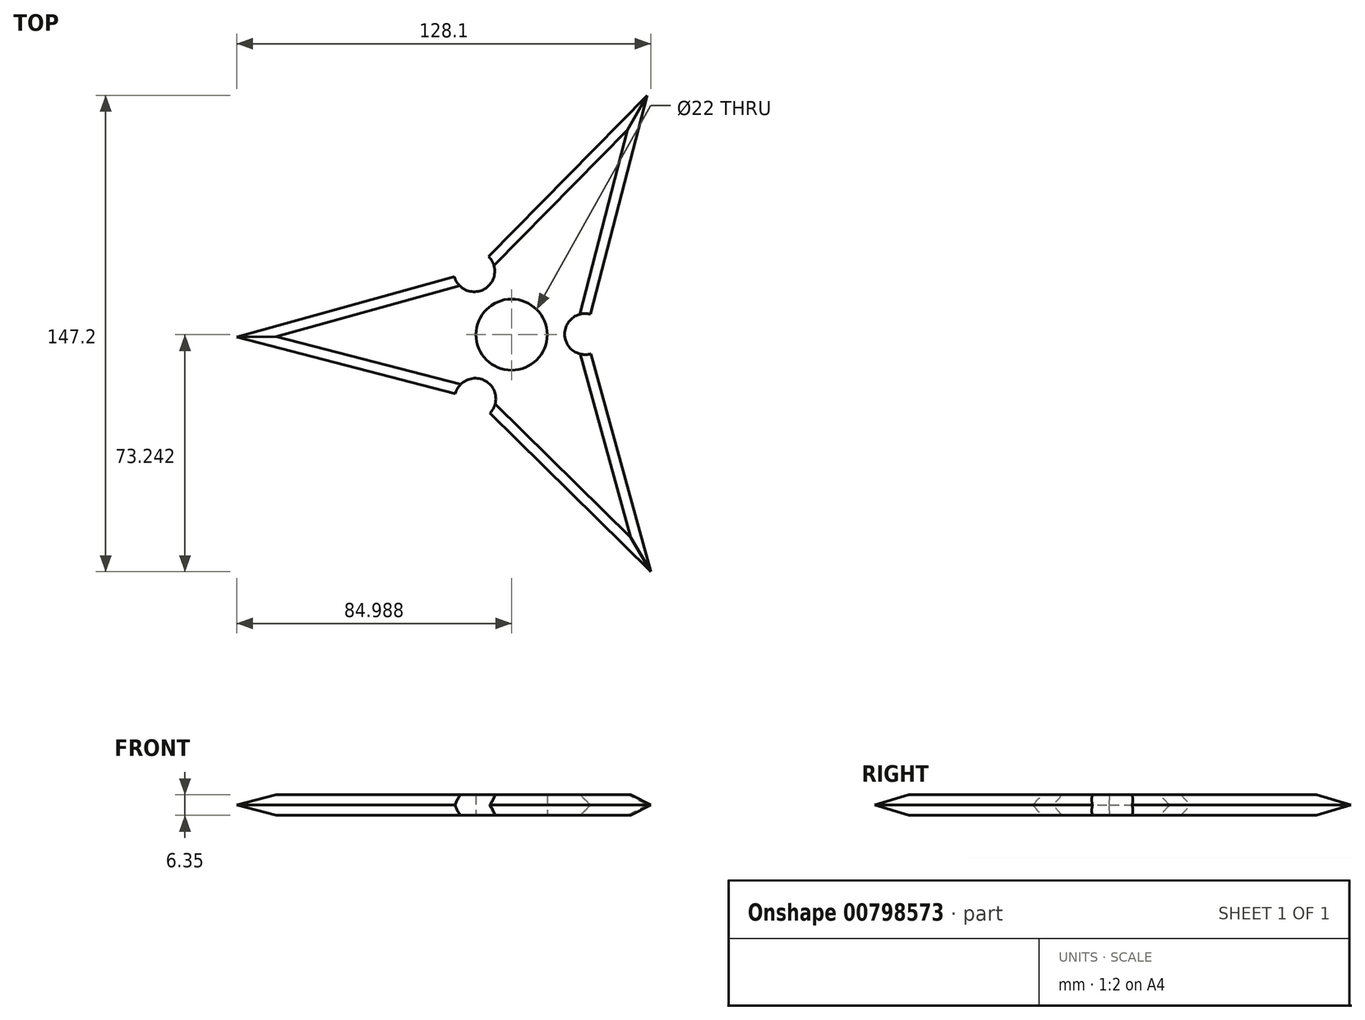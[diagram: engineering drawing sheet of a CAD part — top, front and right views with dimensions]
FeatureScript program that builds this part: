
annotation { "Feature Type Name" : "Feature", "Feature Type Description" : "" }
export const myFeature = defineFeature(function(context is Context, id is Id, definition is map)
    precondition{}
    {
        {
            var Q0;
            Q0=qCreatedBy(makeId("Top.planeOp"),FACE);
            var sketch = newSketch(context, id + "F0", { "sketchPlane" : qUnion([Q0])});
            skLineSegment(sketch, "E0", {"start": v(19.1, 47.74) * mm, "end": v(-34.32, -6.6) * mm});
            skLineSegment(sketch, "E1", {"start": v(-34.32, -6.6) * mm, "end": v(-107.76, -26.93) * mm});
            skLineSegment(sketch, "E2", {"start": v(-107.76, -26.93) * mm, "end": v(-34, -46.04) * mm});
            skLineSegment(sketch, "E3", {"start": v(-34, -46.04) * mm, "end": v(20.34, -99.46) * mm});
            skLineSegment(sketch, "E4", {"start": v(20.34, -99.46) * mm, "end": v(0, -26.03) * mm});
            skLineSegment(sketch, "E5", {"start": v(0, -26.03) * mm, "end": v(19.1, 47.74) * mm});
            skLineSegment(sketch, "E6", {"start": v(-34.32, -6.6) * mm, "end": v(20.34, -99.46) * mm});
            skLineSegment(sketch, "E7", {"start": v(-34, -46.04) * mm, "end": v(19.1, 47.74) * mm});
            skLineSegment(sketch, "E8", {"start": v(0, -26.03) * mm, "end": v(-107.76, -26.93) * mm});
            skCircle(sketch, "E9", {"center": v(-34.32, -6.6) * mm, "radius": 6.35 * mm});
            skCircle(sketch, "E10", {"center": v(-22.77, -26.22) * mm, "radius": 11 * mm});
            skCircle(sketch, "E11", {"center": v(0, -26.03) * mm, "radius": 6.35 * mm});
            skCircle(sketch, "E12", {"center": v(-34, -46.04) * mm, "radius": 6.35 * mm});
            skSolve(sketch);
        }
        {
            var Q0;
            {var subQ0=sQuery(id+"F0.wireOp",EDGE,"E9");var subQ3=sQuery(id+"F0.wireOp",EDGE,"E6");var subQ4=makeQuery(id+"F0.imprint","INTERSECT",VERTEX,{"derivedFrom":[subQ3,subQ0]});Q0=makeQuery(id+"F0.imprint","IMPRINT",FACE,{"disambiguationData":[TD([[makeQuery(id+"F0.imprint","IMPRINT",EDGE,{"disambiguationData":[TD([[subQ4,-1.0]])],"derivedFrom":subQ3}),1.0]])]});}
            var Q1;
            {var subQ5=sQuery(id+"F0.wireOp",EDGE,"E9");var subQ7=sQuery(id+"F0.wireOp",EDGE,"E6");var subQ8=makeQuery(id+"F0.imprint","INTERSECT",VERTEX,{"derivedFrom":[subQ7,subQ5]});Q1=makeQuery(id+"F0.imprint","IMPRINT",FACE,{"disambiguationData":[TD([[makeQuery(id+"F0.imprint","IMPRINT",EDGE,{"disambiguationData":[TD([[subQ8,-1.0]])],"derivedFrom":subQ7}),-1.0]])]});}
            var Q2;
            {var subQ5=sQuery(id+"F0.wireOp",EDGE,"E12");var subQ7=sQuery(id+"F0.wireOp",EDGE,"E7");var subQ9=makeQuery(id+"F0.imprint","INTERSECT",VERTEX,{"derivedFrom":[subQ7,subQ5]});Q2=makeQuery(id+"F0.imprint","IMPRINT",FACE,{"disambiguationData":[TD([[makeQuery(id+"F0.imprint","IMPRINT",EDGE,{"disambiguationData":[TD([[subQ9,-1.0]])],"derivedFrom":subQ7}),1.0]])]});}
            var Q3;
            {var subQ3=sQuery(id+"F0.wireOp",EDGE,"E7");var subQ5=sQuery(id+"F0.wireOp",EDGE,"E12");var subQ6=makeQuery(id+"F0.imprint","INTERSECT",VERTEX,{"derivedFrom":[subQ3,subQ5]});Q3=makeQuery(id+"F0.imprint","IMPRINT",FACE,{"disambiguationData":[TD([[makeQuery(id+"F0.imprint","IMPRINT",EDGE,{"disambiguationData":[TD([[subQ6,-1.0]])],"derivedFrom":subQ3}),-1.0]])]});}
            var Q4;
            {var subQ3=sQuery(id+"F0.wireOp",EDGE,"E8");var subQ7=sQuery(id+"F0.wireOp",EDGE,"E11");var subQ8=makeQuery(id+"F0.imprint","INTERSECT",VERTEX,{"derivedFrom":[subQ3,subQ7]});Q4=makeQuery(id+"F0.imprint","IMPRINT",FACE,{"disambiguationData":[TD([[makeQuery(id+"F0.imprint","IMPRINT",EDGE,{"disambiguationData":[TD([[subQ8,-1.0]])],"derivedFrom":subQ3}),1.0]])]});}
            var Q5;
            {var subQ3=sQuery(id+"F0.wireOp",EDGE,"E8");var subQ5=sQuery(id+"F0.wireOp",EDGE,"E11");var subQ6=makeQuery(id+"F0.imprint","INTERSECT",VERTEX,{"derivedFrom":[subQ3,subQ5]});Q5=makeQuery(id+"F0.imprint","IMPRINT",FACE,{"disambiguationData":[TD([[makeQuery(id+"F0.imprint","IMPRINT",EDGE,{"disambiguationData":[TD([[subQ6,-1.0]])],"derivedFrom":subQ3}),-1.0]])]});}
            extrude(context, id + "F1", {"entities" : qUnion([Q0, Q1, Q2, Q3, Q4, Q5]), "depth" : 6.35 * mm, "offsetDistance" : 30.48 * mm});
        }
        {
            var Q0;
            Q0=makeQuery(id+"F1.opExtrude","CAP_EDGE",EDGE,{"disambiguationData":[OSD([sQuery(id+"F0.wireOp",EDGE,"E1")])],"isStart":false});
            var Q1;
            Q1=makeQuery(id+"F1.opExtrude","CAP_EDGE",EDGE,{"disambiguationData":[OSD([sQuery(id+"F0.wireOp",EDGE,"E2")])],"isStart":false});
            var Q2;
            Q2=makeQuery(id+"F1.opExtrude","CAP_EDGE",EDGE,{"disambiguationData":[OSD([sQuery(id+"F0.wireOp",EDGE,"E2")])],"isStart":true});
            var Q3;
            Q3=makeQuery(id+"F1.opExtrude","CAP_EDGE",EDGE,{"disambiguationData":[OSD([sQuery(id+"F0.wireOp",EDGE,"E3")])],"isStart":false});
            var Q4;
            Q4=makeQuery(id+"F1.opExtrude","CAP_EDGE",EDGE,{"disambiguationData":[OSD([sQuery(id+"F0.wireOp",EDGE,"E4")])],"isStart":false});
            var Q5;
            Q5=makeQuery(id+"F1.opExtrude","CAP_EDGE",EDGE,{"disambiguationData":[OSD([sQuery(id+"F0.wireOp",EDGE,"E0")])],"isStart":false});
            var Q6;
            Q6=makeQuery(id+"F1.opExtrude","CAP_EDGE",EDGE,{"disambiguationData":[OSD([sQuery(id+"F0.wireOp",EDGE,"E1")])],"isStart":true});
            var Q7;
            Q7=makeQuery(id+"F1.opExtrude","CAP_EDGE",EDGE,{"disambiguationData":[OSD([sQuery(id+"F0.wireOp",EDGE,"E3")])],"isStart":true});
            var Q8;
            Q8=makeQuery(id+"F1.opExtrude","CAP_EDGE",EDGE,{"disambiguationData":[OSD([sQuery(id+"F0.wireOp",EDGE,"E4")])],"isStart":true});
            var Q9;
            Q9=makeQuery(id+"F1.opExtrude","CAP_EDGE",EDGE,{"disambiguationData":[OSD([sQuery(id+"F0.wireOp",EDGE,"E0")])],"isStart":true});
            var Q10;
            Q10=makeQuery(id+"F1.opExtrude","CAP_EDGE",EDGE,{"disambiguationData":[OSD([sQuery(id+"F0.wireOp",EDGE,"E5")])],"isStart":true});
            var Q11;
            Q11=makeQuery(id+"F1.opExtrude","CAP_EDGE",EDGE,{"disambiguationData":[OSD([sQuery(id+"F0.wireOp",EDGE,"E5")])],"isStart":false});
            chamfer(context, id + "F2", {"entities" : qUnion([Q0, Q1, Q2, Q3, Q4, Q5, Q6, Q7, Q8, Q9, Q10, Q11]), "width" : 3.17 * mm, "tangentPropagation" : true});
        }
    });
